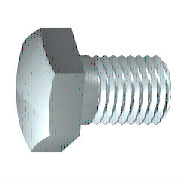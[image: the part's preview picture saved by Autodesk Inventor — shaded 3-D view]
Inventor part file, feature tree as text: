
AUTODESK INVENTOR PART (.ipt)
format: ipt  version: 2025.1 (Build 291241020, 241B)  size: 198,144 bytes
history: native  units: mm (DEFAULTED — no unit token found)
features: extrude x1, chamfer x1, plane x1
ambient origin geometry x7: Origin, YZ Plane, XZ Plane, X Axis, Y Axis, Z Axis, Center Point
bodies: Solid1 (feature_tree), Body (feature_tree)
feature tree (3):
  extrude  "Head"  Depth=35.0mm
  chamfer  "Chamfer1"  Distance=30.5mm
  plane  "Work Plane1"
